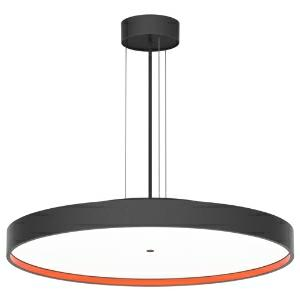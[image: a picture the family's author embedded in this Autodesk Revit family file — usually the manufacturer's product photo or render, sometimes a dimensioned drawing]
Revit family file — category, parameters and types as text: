
# Revit family: sign_diva_410-8310
name_source: partatom
category: Lighting Fixtures
units: mm (PartAtom-declared; Revit-internal decimal feet)

## family parameters
Cut with Voids When Loaded = No
Host = Face
Light Source = No
Part Type = Normal
Room Calculation Point = No
Round Connector Dimension = Use Diameter
Shared = No

## types (1)
- 410-8310-D01-H27-S27 (1 x LED, 9229.8 lm, 2700K)
    Apparent Load = 68 VA
    CIE Flux Codes = 46 76 93 80 73
    Color Rendering = 1A/90…99
    Color Temperature = 2700K
    Default Elevation = 1800 mm
    Description = SIGN DIVA
    Height = 86 mm
    Lamp = 1 x LED
    Lamp Light Flux = 9229.8 lm
    Lamp count = 1
    Length = 570 mm
    Luminous efficacy = 99 lm/W
    Manufacturer = Prolicht
    ModVariant = No
    Model = 410-8310
    Mounting Place = Ceiling
    Mounting Type = Pendant
    Number of Poles = 1
    OnlyDefault = Yes
    Power Factor = 1
    Product Name = SIGN DIVA
    Product group = Suspended lights
    ProductGroupID = 941
    Protection Class = Protection class
    Protection Degree = Degree of protection
    RLX_Detail_Level = 1
    RLX_Emergency_Light_Flux = 0 lm
    RLX_Emergency_Type = 0
    RLX_Emergency_Type_DB = No
    RlxData = <blob elided: 225565 chars, md5=20d49cde>
    Socket = socket
    Standby Power = 0 W
    System Light Flux = 6729 lm
    System Power = 68 W
    Type Comments = DIFFUSER Opal (01),LED COLOUR DIR 2700 K (27),LED COLOUR IND 2700 K (27)
    Type Image = 410-8310.jpg
    URL = http://relux.com
    VarID = 410-8310-d01-h27-s27
    Voltage = 0 V
    Weight = 0.00 kg
    Width = 0 mm  [stored 0 ft]

note: [stored X ft] marks values corroborated as IEEE doubles in the binary element streams (Revit-internal decimal feet)

## geometry (parser evidence)
native form markers: Blend x4, Sweep x13
no freeform markers — native parametric forms only
